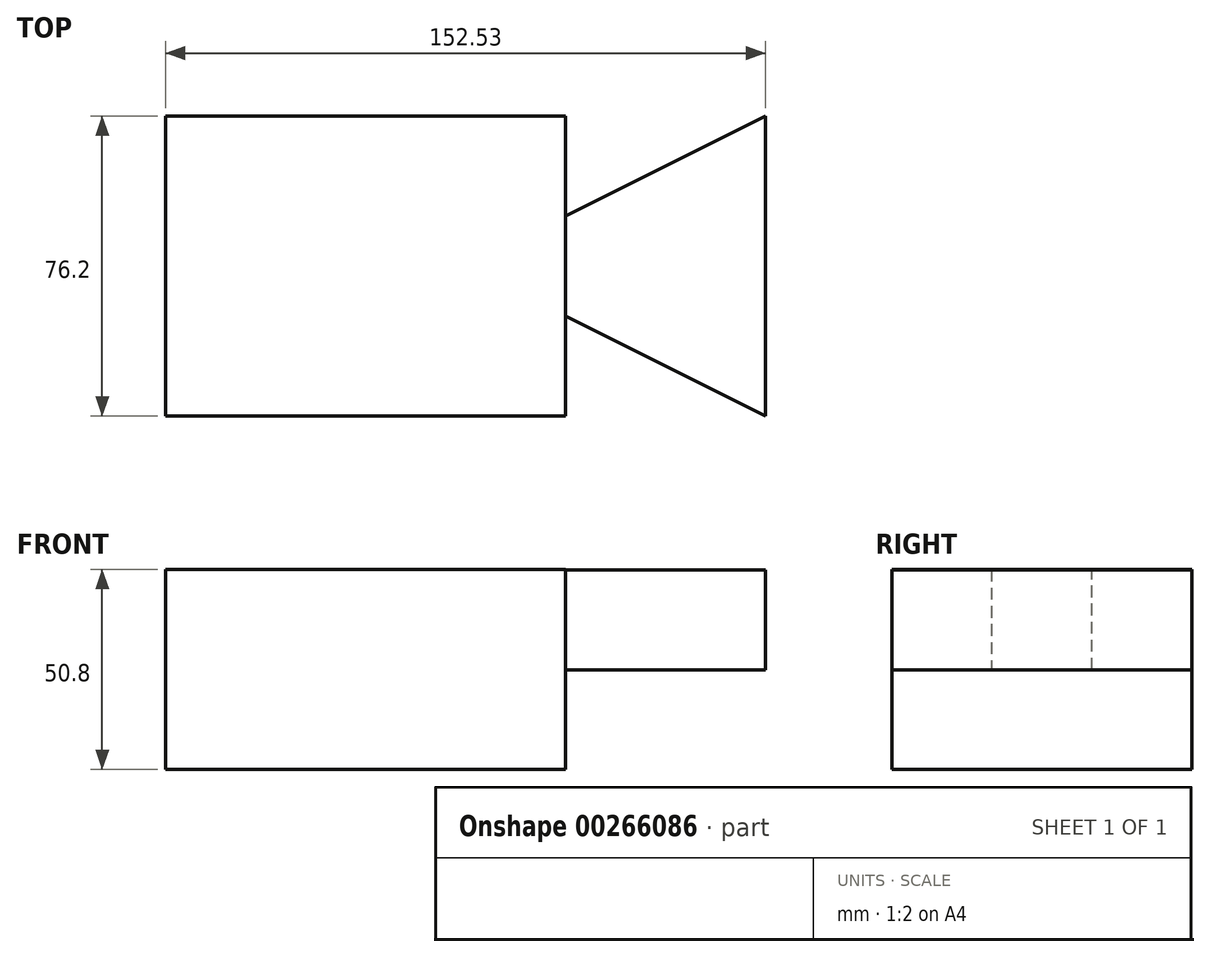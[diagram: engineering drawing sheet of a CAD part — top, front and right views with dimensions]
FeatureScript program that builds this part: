
annotation { "Feature Type Name" : "Feature", "Feature Type Description" : "" }
export const myFeature = defineFeature(function(context is Context, id is Id, definition is map)
    precondition{}
    {
        {
            var Q0;
            Q0=qCreatedBy(makeId("Front.planeOp"),FACE);
            var sketch = newSketch(context, id + "F0", { "sketchPlane" : qUnion([Q0])});
            skLineSegment(sketch, "E0.bottom", {"start": v(-51.8, 25.47) * mm, "end": v(49.8, 25.47) * mm});
            skLineSegment(sketch, "E0.top", {"start": v(-51.8, -25.33) * mm, "end": v(49.8, -25.33) * mm});
            skLineSegment(sketch, "E0.left", {"start": v(-51.8, 25.47) * mm, "end": v(-51.8, -25.33) * mm});
            skLineSegment(sketch, "E0.right", {"start": v(49.8, 25.47) * mm, "end": v(49.8, -25.33) * mm});
            skSolve(sketch);
        }
        {
            var Q0;
            Q0 = qSketchRegion(id + "F0", true);
            extrude(context, id + "F1", {"entities" : qUnion([Q0]), "depth" : 76.2 * mm});
        }
        {
            var Q0;
            Q0=qCreatedBy(makeId("Top.planeOp"),FACE);
            var sketch = newSketch(context, id + "F2", { "sketchPlane" : qUnion([Q0])});
            skLineSegment(sketch, "E1", {"start": v(49.8, -76.2) * mm, "end": v(49.8, -50.8) * mm});
            skLineSegment(sketch, "E2", {"start": v(49.8, -50.8) * mm, "end": v(49.5, -25.4) * mm});
            skLineSegment(sketch, "E3", {"start": v(49.8, -76.2) * mm, "end": v(100.6, -76.2) * mm});
            skLineSegment(sketch, "E4", {"start": v(49.8, -50.8) * mm, "end": v(100.6, -76.2) * mm});
            skLineSegment(sketch, "E5", {"start": v(100.6, 0) * mm, "end": v(49.8, -25.4) * mm});
            skLineSegment(sketch, "E6", {"start": v(49.8, -25.4) * mm, "end": v(49.8, 0) * mm});
            skLineSegment(sketch, "E7", {"start": v(49.8, 0) * mm, "end": v(100.6, 0) * mm});
            skSolve(sketch);
        }
        {
            var Q0;
            Q0=qCreatedBy(makeId("Top.planeOp"),FACE);
            var sketch = newSketch(context, id + "F3", { "sketchPlane" : qUnion([Q0])});
            skLineSegment(sketch, "E8.bottom", {"start": v(49.92, 0) * mm, "end": v(100.72, 0) * mm});
            skLineSegment(sketch, "E8.top", {"start": v(49.92, -76.2) * mm, "end": v(100.72, -76.2) * mm});
            skLineSegment(sketch, "E8.left", {"start": v(49.92, 0) * mm, "end": v(49.92, -76.2) * mm});
            skLineSegment(sketch, "E8.right", {"start": v(100.72, 0) * mm, "end": v(100.72, -76.2) * mm});
            skSolve(sketch);
        }
        {
            var Q0;
            Q0=makeQuery(id+"F3.imprint","IMPRINT",FACE,{"disambiguationData":[TD([[makeQuery(id+"F3.imprint","IMPRINT",EDGE,{"derivedFrom":sQuery(id+"F3.wireOp",EDGE,"E8.bottom")}),-1.0]])]});
            extrude(context, id + "F4", {"entities" : qUnion([Q0]), "depth" : 25.4 * mm});
        }
        {
            var Q0;
            Q0=makeQuery(id+"F2.imprint","IMPRINT",FACE,{"disambiguationData":[TD([[makeQuery(id+"F2.imprint","IMPRINT",EDGE,{"derivedFrom":sQuery(id+"F2.wireOp",EDGE,"E5")}),-1.0]])]});
            var Q1;
            Q1=makeQuery(id+"F2.imprint","IMPRINT",FACE,{"disambiguationData":[TD([[makeQuery(id+"F2.imprint","IMPRINT",EDGE,{"derivedFrom":sQuery(id+"F2.wireOp",EDGE,"E1")}),-1.0]])]});
            extrude(context, id + "F5", {"entities" : qUnion([Q0, Q1]), "operationType" : NewBodyOperationType.REMOVE, "endBound" : BoundingType.UP_TO_NEXT, "depth" : 25.4 * mm});
        }
    });
